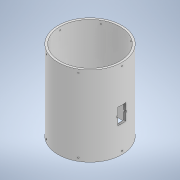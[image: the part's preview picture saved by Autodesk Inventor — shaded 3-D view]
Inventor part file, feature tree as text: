
AUTODESK INVENTOR PART (.ipt)
format: ipt  version: 2022 (Build 260153000, 153)  size: 199,680 bytes
history: native  units: mm
features: extrude x4, plane x4, sketch x4, pattern_circular x1, mirror x1
ambient origin geometry x8: Origin, YZ Plane, XZ Plane, XY Plane, X Axis, Y Axis, Z Axis, Center Point
bodies: Solid1 (feature_tree)
feature tree (14):
  extrude  "Extrusion1"  Depth=40.0mm
  plane  "Work Plane3"
  extrude  "Extrusion9"  [1 undecoded]
  extrude  "Extrusion10"  Depth=5.0mm
  plane  "Work Plane4"
  plane  "Work Plane5"
  extrude  "Extrusion13"  Depth=10.0mm TaperAngle=0.0deg
  pattern_circular  "Circular Pattern1"  [2 undecoded]
  plane  "Work Plane6"
  mirror  "Mirror2"
  sketch  "Sketch1"  dims[d0=37.47mm d1=40.0mm]
  sketch  "Sketch8"  dims[d2=50.0mm d3=0.0mm d34=-21.88mm]
  sketch  "Sketch9"  dims[d35=3.0mm d36=5.0mm]
  sketch  "Sketch13"  dims[d37=2.5mm d40=10.0mm d41=0.0mm d42=3.0mm d43=6.0mm d44=3.0mm d46=18.0mm d47=1.0mm d48=0.0mm d64=0.75mm d65=0.0mm d66=0.0mm d67=60.0mm d68=360.0deg d70=2.0mm d6=0.5mm d7=0.872665mm d8=0.5mm d9=0.872665mm d49=0.5mm d50=0.872665mm]
note: 3 required parameter values undecoded (feature->parameter linkage not recoverable at this tier; creation-order binding heuristic only, values carry confidence <= 0.55)
